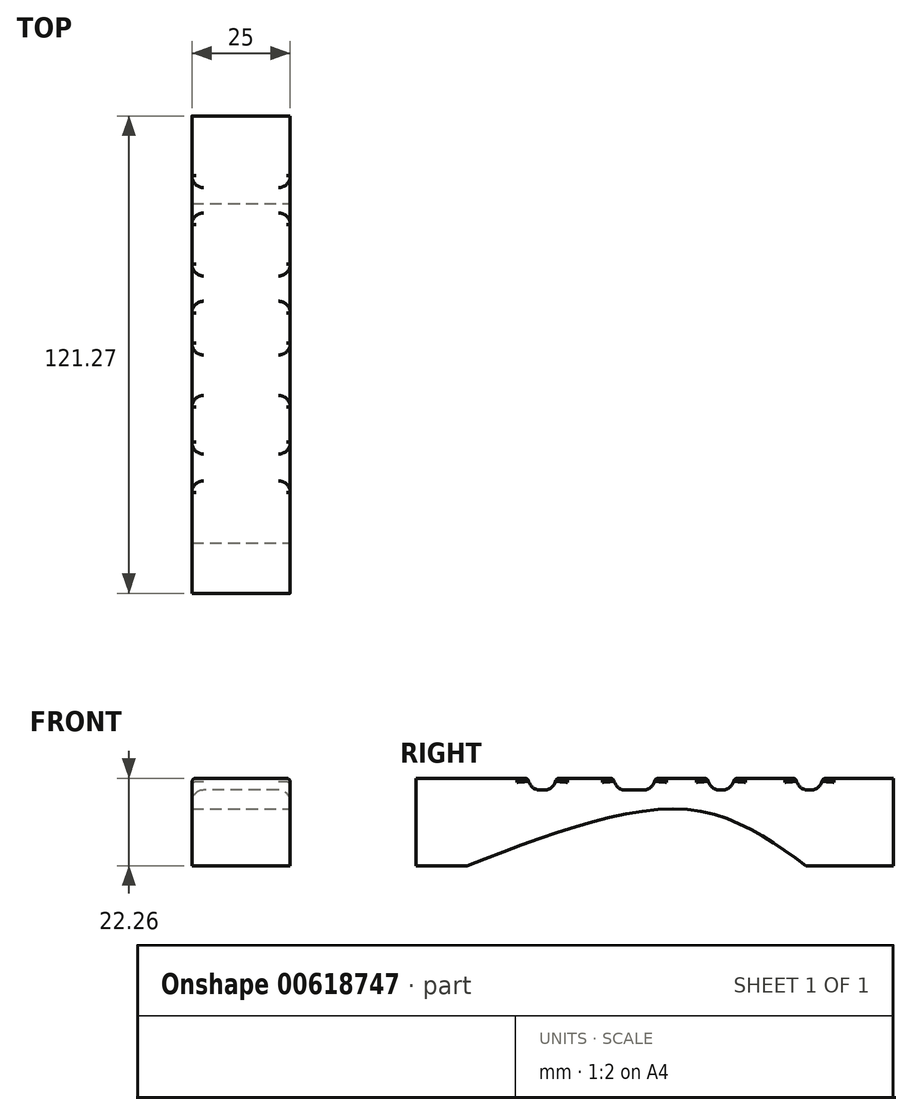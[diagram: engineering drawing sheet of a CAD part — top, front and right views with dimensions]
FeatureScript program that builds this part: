
annotation { "Feature Type Name" : "Feature", "Feature Type Description" : "" }
export const myFeature = defineFeature(function(context is Context, id is Id, definition is map)
    precondition{}
    {
        {
            var Q0;
            Q0=qCreatedBy(makeId("Right.planeOp"),FACE);
            var sketch = newSketch(context, id + "F0", { "sketchPlane" : qUnion([Q0])});
            skLineSegment(sketch, "E0.bottom", {"start": v(0, 0) * mm, "end": v(121.27, 0) * mm});
            skLineSegment(sketch, "E0.top", {"start": v(0, 22.26) * mm, "end": v(121.27, 22.26) * mm});
            skLineSegment(sketch, "E0.left", {"start": v(0, 0) * mm, "end": v(0, 22.26) * mm});
            skLineSegment(sketch, "E0.right", {"start": v(121.27, 0) * mm, "end": v(121.27, 22.26) * mm});
            skFitSpline(sketch, "E1", {"points": [v(99.02, 0) * mm, v(69.34, 14.27) * mm, v(12.84, 0) * mm], "startDerivative": vector(-62.76, 45.74) * mm, "endDerivative": vector(-107.48, -41.62) * mm});
            skSolve(sketch);
        }
        {
            var Q0;
            Q0=makeQuery(id+"F0.imprint","IMPRINT",FACE,{"disambiguationData":[TD([[makeQuery(id+"F0.imprint","IMPRINT",EDGE,{"derivedFrom":sQuery(id+"F0.wireOp",EDGE,"E0.top")}),-1.0]])]});
            extrude(context, id + "F1", {"entities" : qUnion([Q0]), "oppositeDirection" : true, "depth" : 25 * mm, "offsetDistance" : 25 * mm});
        }
        {
            var Q0;
            Q0=makeQuery(id+"F1.opExtrude","SWEPT_FACE",FACE,{"disambiguationData":[OSD([sQuery(id+"F0.wireOp",EDGE,"E0.top")])]});
            var sketch = newSketch(context, id + "F2", { "sketchPlane" : qUnion([Q0])});
            skLineSegment(sketch, "E2", {"start": v(-25, 28.47) * mm, "end": v(0, 28.47) * mm});
            skLineSegment(sketch, "E3", {"start": v(0, 28.47) * mm, "end": v(0, 35.46) * mm});
            skLineSegment(sketch, "E4", {"start": v(0, 35.46) * mm, "end": v(-25, 35.46) * mm});
            skLineSegment(sketch, "E5", {"start": v(-25, 35.46) * mm, "end": v(-25, 28.47) * mm});
            skLineSegment(sketch, "E6", {"start": v(-25, 50.18) * mm, "end": v(0, 50.18) * mm});
            skLineSegment(sketch, "E7", {"start": v(0, 50.18) * mm, "end": v(0, 60.64) * mm});
            skLineSegment(sketch, "E8", {"start": v(0, 60.64) * mm, "end": v(-25, 60.64) * mm});
            skLineSegment(sketch, "E9", {"start": v(-25, 60.64) * mm, "end": v(-25, 50.18) * mm});
            skLineSegment(sketch, "E10", {"start": v(-25, 74.1) * mm, "end": v(0, 74.1) * mm});
            skLineSegment(sketch, "E11", {"start": v(0, 74.1) * mm, "end": v(0, 80.73) * mm});
            skLineSegment(sketch, "E12", {"start": v(0, 80.73) * mm, "end": v(-25, 80.73) * mm});
            skLineSegment(sketch, "E13", {"start": v(-25, 80.73) * mm, "end": v(-25, 74.1) * mm});
            skLineSegment(sketch, "E14", {"start": v(-25, 96.55) * mm, "end": v(0, 96.55) * mm});
            skLineSegment(sketch, "E15", {"start": v(0, 96.55) * mm, "end": v(0, 103.17) * mm});
            skLineSegment(sketch, "E16", {"start": v(0, 103.17) * mm, "end": v(-25, 103.17) * mm});
            skLineSegment(sketch, "E17", {"start": v(-25, 103.17) * mm, "end": v(-25, 96.55) * mm});
            skSolve(sketch);
        }
        {
            var Q0;
            Q0 = qSketchRegion(id + "F2", true);
            extrude(context, id + "F3", {"entities" : qUnion([Q0]), "operationType" : NewBodyOperationType.REMOVE, "oppositeDirection" : true, "depth" : 3 * mm, "offsetDistance" : 25 * mm});
        }
        {
            var Q0;
            Q0=makeQuery(id+"F3.boolean.opBoolean","COPY",FACE,{"derivedFrom":makeQuery(id+"F3.opExtrude","CAP_FACE",FACE,{"disambiguationData":[OSD([sQuery(id+"F2.wireOp",EDGE,"E2"),sQuery(id+"F2.wireOp",EDGE,"E3"),sQuery(id+"F2.wireOp",EDGE,"E4"),sQuery(id+"F2.wireOp",EDGE,"E5")])],"isStart":false})});
            var Q1;
            Q1=makeQuery(id+"F3.boolean.opBoolean","COPY",FACE,{"derivedFrom":makeQuery(id+"F3.opExtrude","CAP_FACE",FACE,{"disambiguationData":[OSD([sQuery(id+"F2.wireOp",EDGE,"E6"),sQuery(id+"F2.wireOp",EDGE,"E7"),sQuery(id+"F2.wireOp",EDGE,"E8"),sQuery(id+"F2.wireOp",EDGE,"E9")])],"isStart":false})});
            var Q2;
            Q2=makeQuery(id+"F3.boolean.opBoolean","COPY",FACE,{"derivedFrom":makeQuery(id+"F3.opExtrude","CAP_FACE",FACE,{"disambiguationData":[OSD([sQuery(id+"F2.wireOp",EDGE,"E10"),sQuery(id+"F2.wireOp",EDGE,"E11"),sQuery(id+"F2.wireOp",EDGE,"E12"),sQuery(id+"F2.wireOp",EDGE,"E13")])],"isStart":false})});
            var Q3;
            Q3=makeQuery(id+"F3.boolean.opBoolean","COPY",FACE,{"derivedFrom":makeQuery(id+"F3.opExtrude","CAP_FACE",FACE,{"disambiguationData":[OSD([sQuery(id+"F2.wireOp",EDGE,"E14"),sQuery(id+"F2.wireOp",EDGE,"E15"),sQuery(id+"F2.wireOp",EDGE,"E16"),sQuery(id+"F2.wireOp",EDGE,"E17")])],"isStart":false})});
            fillet(context, id + "F4", {"entities" : qUnion([Q0, Q1, Q2, Q3]), "radius" : 3 * mm, "tangentPropagation" : true, "allowEdgeOverflow" : false});
        }
        {
            var Q0;
            {var subQ2=sQuery(id+"F0.wireOp",EDGE,"E0.left");var subQ3=sQuery(id+"F0.wireOp",EDGE,"E0.top");var subQ5=sQuery(id+"F2.wireOp",EDGE,"E2");Q0=makeQuery(id+"F4.opFillet","BLEND_EDGE",EDGE,{"blendedFrom":[makeQuery(id+"F3.boolean.opBoolean","COPY",EDGE,{"derivedFrom":makeQuery(id+"F3.opExtrude","CAP_EDGE",EDGE,{"disambiguationData":[OSD([subQ5])],"isStart":false})}),makeQuery(id+"F3.boolean.opBoolean","SPLIT",FACE,{"disambiguationData":[TD([makeQuery(id+"F1.opExtrude","SWEPT_FACE",FACE,{"disambiguationData":[OSD([subQ2])]})])],"derivedFrom":makeQuery(id+"F1.opExtrude","SWEPT_FACE",FACE,{"disambiguationData":[OSD([subQ3])]})})],"blendedInto":[makeQuery(id+"F3.boolean.opBoolean","SPLIT",FACE,{"disambiguationData":[TD([makeQuery(id+"F1.opExtrude","SWEPT_FACE",FACE,{"disambiguationData":[OSD([subQ2])]})])],"derivedFrom":makeQuery(id+"F1.opExtrude","SWEPT_FACE",FACE,{"disambiguationData":[OSD([subQ3])]})})]});}
            var Q1;
            {var subQ3=sQuery(id+"F0.wireOp",EDGE,"E0.top");var subQ5=sQuery(id+"F2.wireOp",EDGE,"E4");Q1=makeQuery(id+"F4.opFillet","BLEND_EDGE",EDGE,{"blendedFrom":[makeQuery(id+"F3.boolean.opBoolean","COPY",EDGE,{"derivedFrom":makeQuery(id+"F3.opExtrude","CAP_EDGE",EDGE,{"disambiguationData":[OSD([subQ5])],"isStart":false})}),makeQuery(id+"F3.boolean.opBoolean","SPLIT",FACE,{"disambiguationData":[TD([makeQuery(id+"F3.opExtrude","SWEPT_FACE",FACE,{"disambiguationData":[OSD([subQ5])]})])],"derivedFrom":makeQuery(id+"F1.opExtrude","SWEPT_FACE",FACE,{"disambiguationData":[OSD([subQ3])]})})],"blendedInto":[makeQuery(id+"F3.boolean.opBoolean","SPLIT",FACE,{"disambiguationData":[TD([makeQuery(id+"F3.opExtrude","SWEPT_FACE",FACE,{"disambiguationData":[OSD([subQ5])]})])],"derivedFrom":makeQuery(id+"F1.opExtrude","SWEPT_FACE",FACE,{"disambiguationData":[OSD([subQ3])]})})]});}
            var Q2;
            {var subQ3=sQuery(id+"F0.wireOp",EDGE,"E0.top");var subQ5=sQuery(id+"F2.wireOp",EDGE,"E6");Q2=makeQuery(id+"F4.opFillet","BLEND_EDGE",EDGE,{"blendedFrom":[makeQuery(id+"F3.boolean.opBoolean","COPY",EDGE,{"derivedFrom":makeQuery(id+"F3.opExtrude","CAP_EDGE",EDGE,{"disambiguationData":[OSD([subQ5])],"isStart":false})}),makeQuery(id+"F3.boolean.opBoolean","SPLIT",FACE,{"disambiguationData":[TD([makeQuery(id+"F3.opExtrude","SWEPT_FACE",FACE,{"disambiguationData":[OSD([sQuery(id+"F2.wireOp",EDGE,"E4")])]})])],"derivedFrom":makeQuery(id+"F1.opExtrude","SWEPT_FACE",FACE,{"disambiguationData":[OSD([subQ3])]})})],"blendedInto":[makeQuery(id+"F3.boolean.opBoolean","SPLIT",FACE,{"disambiguationData":[TD([makeQuery(id+"F3.opExtrude","SWEPT_FACE",FACE,{"disambiguationData":[OSD([sQuery(id+"F2.wireOp",EDGE,"E4")])]})])],"derivedFrom":makeQuery(id+"F1.opExtrude","SWEPT_FACE",FACE,{"disambiguationData":[OSD([subQ3])]})})]});}
            var Q3;
            {var subQ3=sQuery(id+"F0.wireOp",EDGE,"E0.top");var subQ5=sQuery(id+"F2.wireOp",EDGE,"E8");Q3=makeQuery(id+"F4.opFillet","BLEND_EDGE",EDGE,{"blendedFrom":[makeQuery(id+"F3.boolean.opBoolean","COPY",EDGE,{"derivedFrom":makeQuery(id+"F3.opExtrude","CAP_EDGE",EDGE,{"disambiguationData":[OSD([subQ5])],"isStart":false})}),makeQuery(id+"F3.boolean.opBoolean","SPLIT",FACE,{"disambiguationData":[TD([makeQuery(id+"F3.opExtrude","SWEPT_FACE",FACE,{"disambiguationData":[OSD([subQ5])]})])],"derivedFrom":makeQuery(id+"F1.opExtrude","SWEPT_FACE",FACE,{"disambiguationData":[OSD([subQ3])]})})],"blendedInto":[makeQuery(id+"F3.boolean.opBoolean","SPLIT",FACE,{"disambiguationData":[TD([makeQuery(id+"F3.opExtrude","SWEPT_FACE",FACE,{"disambiguationData":[OSD([subQ5])]})])],"derivedFrom":makeQuery(id+"F1.opExtrude","SWEPT_FACE",FACE,{"disambiguationData":[OSD([subQ3])]})})]});}
            var Q4;
            {var subQ3=sQuery(id+"F0.wireOp",EDGE,"E0.top");var subQ5=sQuery(id+"F2.wireOp",EDGE,"E10");Q4=makeQuery(id+"F4.opFillet","BLEND_EDGE",EDGE,{"blendedFrom":[makeQuery(id+"F3.boolean.opBoolean","COPY",EDGE,{"derivedFrom":makeQuery(id+"F3.opExtrude","CAP_EDGE",EDGE,{"disambiguationData":[OSD([subQ5])],"isStart":false})}),makeQuery(id+"F3.boolean.opBoolean","SPLIT",FACE,{"disambiguationData":[TD([makeQuery(id+"F3.opExtrude","SWEPT_FACE",FACE,{"disambiguationData":[OSD([sQuery(id+"F2.wireOp",EDGE,"E8")])]})])],"derivedFrom":makeQuery(id+"F1.opExtrude","SWEPT_FACE",FACE,{"disambiguationData":[OSD([subQ3])]})})],"blendedInto":[makeQuery(id+"F3.boolean.opBoolean","SPLIT",FACE,{"disambiguationData":[TD([makeQuery(id+"F3.opExtrude","SWEPT_FACE",FACE,{"disambiguationData":[OSD([sQuery(id+"F2.wireOp",EDGE,"E8")])]})])],"derivedFrom":makeQuery(id+"F1.opExtrude","SWEPT_FACE",FACE,{"disambiguationData":[OSD([subQ3])]})})]});}
            var Q5;
            {var subQ3=sQuery(id+"F0.wireOp",EDGE,"E0.top");var subQ5=sQuery(id+"F2.wireOp",EDGE,"E12");Q5=makeQuery(id+"F4.opFillet","BLEND_EDGE",EDGE,{"blendedFrom":[makeQuery(id+"F3.boolean.opBoolean","COPY",EDGE,{"derivedFrom":makeQuery(id+"F3.opExtrude","CAP_EDGE",EDGE,{"disambiguationData":[OSD([subQ5])],"isStart":false})}),makeQuery(id+"F3.boolean.opBoolean","SPLIT",FACE,{"disambiguationData":[TD([makeQuery(id+"F3.opExtrude","SWEPT_FACE",FACE,{"disambiguationData":[OSD([subQ5])]})])],"derivedFrom":makeQuery(id+"F1.opExtrude","SWEPT_FACE",FACE,{"disambiguationData":[OSD([subQ3])]})})],"blendedInto":[makeQuery(id+"F3.boolean.opBoolean","SPLIT",FACE,{"disambiguationData":[TD([makeQuery(id+"F3.opExtrude","SWEPT_FACE",FACE,{"disambiguationData":[OSD([subQ5])]})])],"derivedFrom":makeQuery(id+"F1.opExtrude","SWEPT_FACE",FACE,{"disambiguationData":[OSD([subQ3])]})})]});}
            var Q6;
            {var subQ3=sQuery(id+"F0.wireOp",EDGE,"E0.top");var subQ5=sQuery(id+"F2.wireOp",EDGE,"E14");Q6=makeQuery(id+"F4.opFillet","BLEND_EDGE",EDGE,{"blendedFrom":[makeQuery(id+"F3.boolean.opBoolean","COPY",EDGE,{"derivedFrom":makeQuery(id+"F3.opExtrude","CAP_EDGE",EDGE,{"disambiguationData":[OSD([subQ5])],"isStart":false})}),makeQuery(id+"F3.boolean.opBoolean","SPLIT",FACE,{"disambiguationData":[TD([makeQuery(id+"F3.opExtrude","SWEPT_FACE",FACE,{"disambiguationData":[OSD([sQuery(id+"F2.wireOp",EDGE,"E12")])]})])],"derivedFrom":makeQuery(id+"F1.opExtrude","SWEPT_FACE",FACE,{"disambiguationData":[OSD([subQ3])]})})],"blendedInto":[makeQuery(id+"F3.boolean.opBoolean","SPLIT",FACE,{"disambiguationData":[TD([makeQuery(id+"F3.opExtrude","SWEPT_FACE",FACE,{"disambiguationData":[OSD([sQuery(id+"F2.wireOp",EDGE,"E12")])]})])],"derivedFrom":makeQuery(id+"F1.opExtrude","SWEPT_FACE",FACE,{"disambiguationData":[OSD([subQ3])]})})]});}
            var Q7;
            {var subQ1=sQuery(id+"F0.wireOp",EDGE,"E0.right");var subQ3=sQuery(id+"F0.wireOp",EDGE,"E0.top");var subQ5=sQuery(id+"F2.wireOp",EDGE,"E16");Q7=makeQuery(id+"F4.opFillet","BLEND_EDGE",EDGE,{"blendedFrom":[makeQuery(id+"F3.boolean.opBoolean","COPY",EDGE,{"derivedFrom":makeQuery(id+"F3.opExtrude","CAP_EDGE",EDGE,{"disambiguationData":[OSD([subQ5])],"isStart":false})}),makeQuery(id+"F3.boolean.opBoolean","SPLIT",FACE,{"disambiguationData":[TD([makeQuery(id+"F1.opExtrude","SWEPT_FACE",FACE,{"disambiguationData":[OSD([subQ1])]})])],"derivedFrom":makeQuery(id+"F1.opExtrude","SWEPT_FACE",FACE,{"disambiguationData":[OSD([subQ3])]})})],"blendedInto":[makeQuery(id+"F3.boolean.opBoolean","SPLIT",FACE,{"disambiguationData":[TD([makeQuery(id+"F1.opExtrude","SWEPT_FACE",FACE,{"disambiguationData":[OSD([subQ1])]})])],"derivedFrom":makeQuery(id+"F1.opExtrude","SWEPT_FACE",FACE,{"disambiguationData":[OSD([subQ3])]})})]});}
            fillet(context, id + "F5", {"entities" : qUnion([Q0, Q1, Q2, Q3, Q4, Q5, Q6, Q7]), "radius" : 1 * mm, "tangentPropagation" : true, "allowEdgeOverflow" : false});
        }
    });
